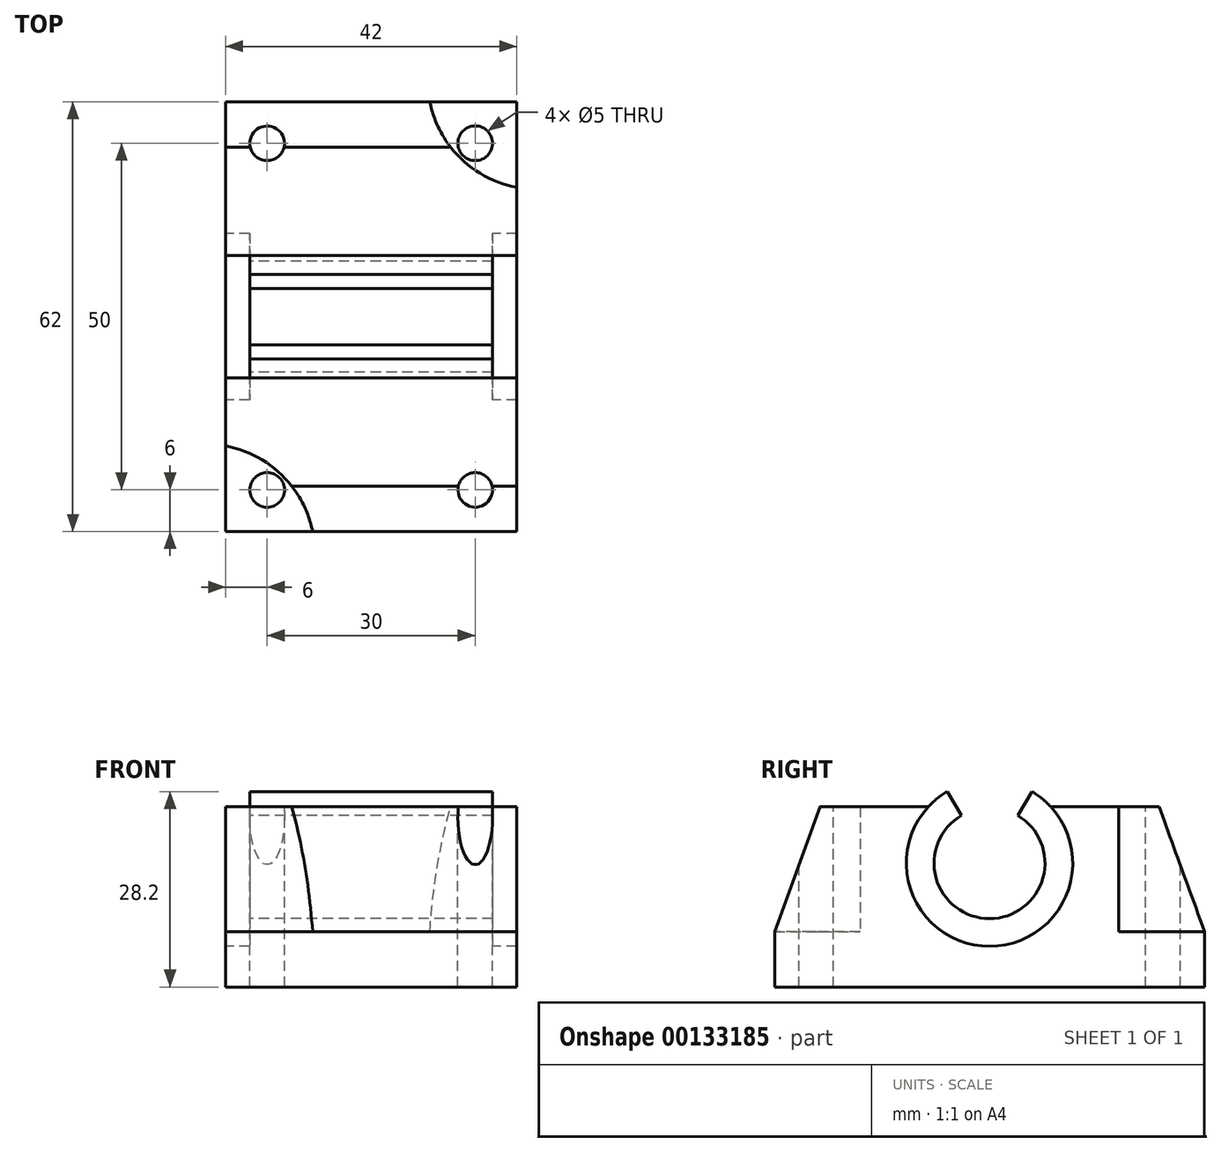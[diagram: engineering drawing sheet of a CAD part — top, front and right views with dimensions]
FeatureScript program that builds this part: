
annotation { "Feature Type Name" : "Feature", "Feature Type Description" : "" }
export const myFeature = defineFeature(function(context is Context, id is Id, definition is map)
    precondition{}
    {
        {
            var Q0;
            Q0=qCreatedBy(makeId("Right.planeOp"),FACE);
            var sketch = newSketch(context, id + "F0", { "sketchPlane" : qUnion([Q0])});
            skCircle(sketch, "E0", {"center": v(0, 0) * mm, "radius": 8 * mm});
            skLineSegment(sketch, "E1", {"start": v(8.82, 8.14) * mm, "end": v(24.45, 8.14) * mm});
            skLineSegment(sketch, "E2", {"start": v(24.45, 8.14) * mm, "end": v(31, -9.86) * mm});
            skLineSegment(sketch, "E3", {"start": v(31, -9.86) * mm, "end": v(31, -17.86) * mm});
            skLineSegment(sketch, "E4", {"start": v(31, -17.86) * mm, "end": v(0, -17.86) * mm});
            skArc(sketch, "E5.0", {"start": v(-6.1, 10.34) * mm, "mid": v(0, -12) * mm, "end": v(6.1, 10.34) * mm});
            skPoint(sketch, "E6.orphan", {"position": v(0, 8.14) * mm});
            skLineSegment(sketch, "E7.MirrorCS", {"start": v(-31, -17.86) * mm, "end": v(0, -17.86) * mm});
            skLineSegment(sketch, "E8.MirrorCS", {"start": v(-31, -9.86) * mm, "end": v(-31, -17.86) * mm});
            skLineSegment(sketch, "E9.MirrorCS", {"start": v(-8.82, 8.14) * mm, "end": v(-24.45, 8.14) * mm});
            skLineSegment(sketch, "E10.MirrorCS", {"start": v(-24.45, 8.14) * mm, "end": v(-31, -9.86) * mm});
            skLineSegment(sketch, "E11", {"start": v(4.06, 6.9) * mm, "end": v(6.1, 10.34) * mm});
            skLineSegment(sketch, "E12.MirrorCS", {"start": v(-4.06, 6.9) * mm, "end": v(-6.1, 10.34) * mm});
            skSolve(sketch);
        }
        {
            var Q0;
            {var subQ0=sQuery(id+"F0.wireOp",EDGE,"E1");Q0=makeQuery(id+"F0.imprint","IMPRINT",FACE,{"disambiguationData":[TD([[makeQuery(id+"F0.imprint","IMPRINT",EDGE,{"derivedFrom":subQ0}),-1.0]])]});}
            extrude(context, id + "F1", {"entities" : qUnion([Q0]), "depth" : 42 * mm, "symmetric" : true});
        }
        {
            var Q0;
            Q0=makeQuery(id+"F1.opExtrude","SWEPT_FACE",FACE,{"disambiguationData":[OSD([sQuery(id+"F0.wireOp",EDGE,"E4"),sQuery(id+"F0.wireOp",EDGE,"E7.MirrorCS")])]});
            cPlane(context, id + "F2", {"entities" : qUnion([Q0]), "cplaneType" : CPlaneType.OFFSET, "offset" : 8 * mm, "oppositeDirection" : true, "width" : 150 * mm, "height" : 150 * mm});
        }
        {
            var Q0;
            Q0=qCreatedBy(id+"F2.planeOp",FACE);
            var sketch = newSketch(context, id + "F3", { "sketchPlane" : qUnion([Q0])});
            skCircle(sketch, "E13", {"center": v(-23.87, 34.13) * mm, "radius": 15.74 * mm});
            skCircle(sketch, "E14.MirrorC", {"center": v(23.87, 34.13) * mm, "radius": 15.74 * mm});
            skCircle(sketch, "E15.MirrorC", {"center": v(-23.87, -34.13) * mm, "radius": 15.74 * mm});
            skCircle(sketch, "E16.MirrorC", {"center": v(23.87, -34.13) * mm, "radius": 15.74 * mm});
            skSolve(sketch);
        }
        {
            var Q0;
            Q0=makeQuery(id+"F3.imprint","IMPRINT",FACE,{"disambiguationData":[TD([[makeQuery(id+"F3.imprint","IMPRINT",EDGE,{"derivedFrom":sQuery(id+"F3.wireOp",EDGE,"E13")}),1.0]])]});
            var Q1;
            Q1=makeQuery(id+"F3.imprint","IMPRINT",FACE,{"disambiguationData":[TD([[makeQuery(id+"F3.imprint","IMPRINT",EDGE,{"derivedFrom":sQuery(id+"F3.wireOp",EDGE,"E15.MirrorC")}),-1.0]])]});
            var Q2;
            Q2=makeQuery(id+"F3.imprint","IMPRINT",FACE,{"disambiguationData":[TD([[makeQuery(id+"F3.imprint","IMPRINT",EDGE,{"derivedFrom":sQuery(id+"F3.wireOp",EDGE,"E16.MirrorC")}),1.0]])]});
            var Q3;
            Q3=makeQuery(id+"F3.imprint","IMPRINT",FACE,{"disambiguationData":[TD([[makeQuery(id+"F3.imprint","IMPRINT",EDGE,{"derivedFrom":sQuery(id+"F3.wireOp",EDGE,"E14.MirrorC")}),-1.0]])]});
            extrude(context, id + "F4", {"entities" : qUnion([Q0, Q1, Q2, Q3]), "operationType" : NewBodyOperationType.REMOVE, "oppositeDirection" : true, "depth" : 33 * mm});
        }
        {
            var Q0;
            {var subQ2=sQuery(id+"F0.wireOp",EDGE,"E11");Q0=makeQuery(id+"F0.imprint","IMPRINT",FACE,{"disambiguationData":[TD([[makeQuery(id+"F0.imprint","IMPRINT",EDGE,{"derivedFrom":subQ2}),-1.0]])]});}
            extrude(context, id + "F5", {"entities" : qUnion([Q0]), "operationType" : NewBodyOperationType.ADD, "depth" : 35 * mm, "symmetric" : true});
        }
        {
            var Q0;
            Q0=makeQuery(id+"F1.opExtrude","SWEPT_FACE",FACE,{"disambiguationData":[OSD([sQuery(id+"F0.wireOp",EDGE,"E4"),sQuery(id+"F0.wireOp",EDGE,"E7.MirrorCS")])]});
            var sketch = newSketch(context, id + "F6", { "sketchPlane" : qUnion([Q0])});
            skPoint(sketch, "E17", {"position": v(-15, -25) * mm});
            skPoint(sketch, "E18.MirrorP", {"position": v(15, -25) * mm});
            skPoint(sketch, "E19.MirrorP", {"position": v(15, 25) * mm});
            skPoint(sketch, "E20.MirrorP", {"position": v(-15, 25) * mm});
            skSolve(sketch);
        }
        {
            var Q0;
            Q0=sQuery(id+"F6.wireOp",VERTEX,"E17");
            var Q1;
            Q1=sQuery(id+"F6.wireOp",VERTEX,"E20.MirrorP");
            var Q2;
            Q2=sQuery(id+"F6.wireOp",VERTEX,"E19.MirrorP");
            var Q3;
            Q3=sQuery(id+"F6.wireOp",VERTEX,"E18.MirrorP");
            var Q4;
            Q4=makeQuery(id+"F1.opExtrude","SWEPT_BODY",BODY,{"disambiguationData":[OSD([sQuery(id+"F0.wireOp",EDGE,"E1"),sQuery(id+"F0.wireOp",EDGE,"E2"),sQuery(id+"F0.wireOp",EDGE,"E3"),sQuery(id+"F0.wireOp",EDGE,"E4"),sQuery(id+"F0.wireOp",EDGE,"E5.0"),sQuery(id+"F0.wireOp",EDGE,"E7.MirrorCS"),sQuery(id+"F0.wireOp",EDGE,"E8.MirrorCS"),sQuery(id+"F0.wireOp",EDGE,"E9.MirrorCS"),sQuery(id+"F0.wireOp",EDGE,"E10.MirrorCS")])]});
            hole(context, id + "F7", {"style" : HoleStyle.SIMPLE, "endStyle" : HoleEndStyle.THROUGH, "holeDiameter" : 5 * mm, "locations" : qUnion([Q0, Q1, Q2, Q3]), "scope" : qUnion([Q4]), "isTappedThrough" : true, "startStyle" : HoleStartStyle.PART});
        }
    });
